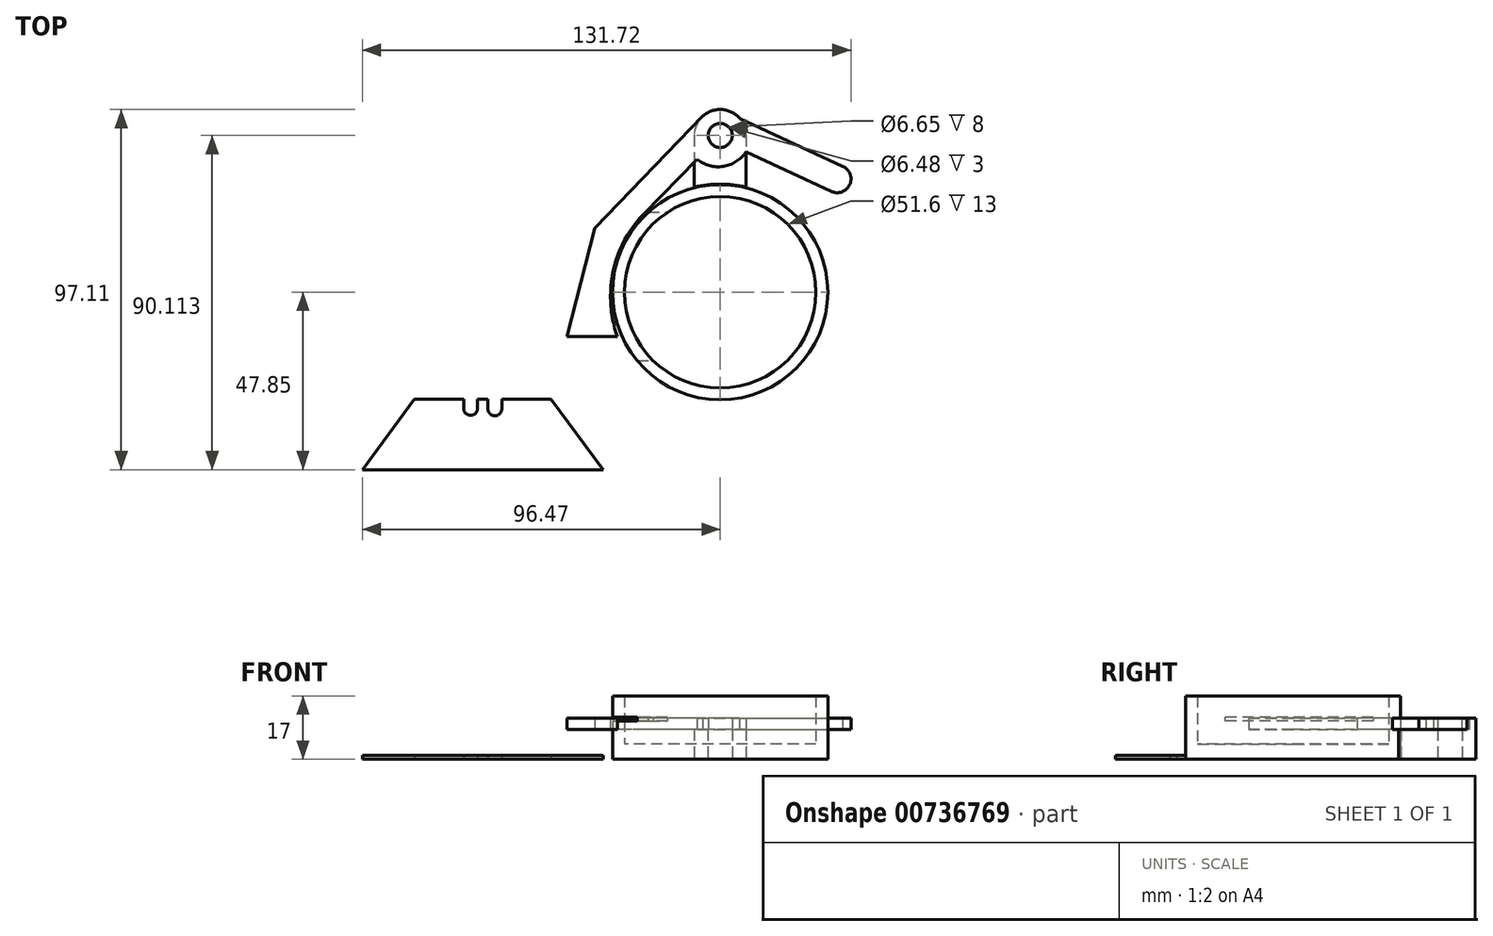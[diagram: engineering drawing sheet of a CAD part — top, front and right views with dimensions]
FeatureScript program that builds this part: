
annotation { "Feature Type Name" : "Feature", "Feature Type Description" : "" }
export const myFeature = defineFeature(function(context is Context, id is Id, definition is map)
    precondition{}
    {
        {
            var Q0;
            Q0=qCreatedBy(makeId("Top.planeOp"),FACE);
            var sketch = newSketch(context, id + "F0", { "sketchPlane" : qUnion([Q0])});
            skCircle(sketch, "E0", {"center": v(0, 0) * mm, "radius": 25.8 * mm});
            skCircle(sketch, "E1", {"center": v(0, 0) * mm, "radius": 29 * mm});
            skSolve(sketch);
        }
        {
            var Q0;
            Q0=makeQuery(id+"F0.imprint","IMPRINT",FACE,{"disambiguationData":[TD([[makeQuery(id+"F0.imprint","IMPRINT",EDGE,{"derivedFrom":sQuery(id+"F0.wireOp",EDGE,"E0")}),1.0]])]});
            extrude(context, id + "F1", {"entities" : qUnion([Q0]), "depth" : 4 * mm, "offsetDistance" : 25 * mm});
        }
        {
            var Q0;
            Q0 = qSketchRegion(id + "F0", true);
            extrude(context, id + "F2", {"entities" : qUnion([Q0]), "operationType" : NewBodyOperationType.ADD, "depth" : 17 * mm, "offsetDistance" : 25 * mm});
        }
        {
            var Q0;
            Q0=qCreatedBy(makeId("Right.planeOp"),FACE);
            var sketch = newSketch(context, id + "F3", { "sketchPlane" : qUnion([Q0])});
            skLineSegment(sketch, "E2.bottom", {"start": v(21.55, 11.3) * mm, "end": v(-18.45, 11.3) * mm});
            skLineSegment(sketch, "E2.top", {"start": v(21.55, 10.3) * mm, "end": v(-18.45, 10.3) * mm});
            skLineSegment(sketch, "E2.left", {"start": v(21.55, 11.3) * mm, "end": v(21.55, 10.3) * mm});
            skLineSegment(sketch, "E2.right", {"start": v(-18.45, 11.3) * mm, "end": v(-18.45, 10.3) * mm});
            skSolve(sketch);
        }
        {
            var Q0;
            Q0 = qSketchRegion(id + "F3", true);
            extrude(context, id + "F4", {"entities" : qUnion([Q0]), "operationType" : NewBodyOperationType.REMOVE, "oppositeDirection" : true, "depth" : 50 * mm, "offsetDistance" : 25 * mm});
        }
        {
            var Q0;
            Q0=qCreatedBy(makeId("Top.planeOp"),FACE);
            var sketch = newSketch(context, id + "F5", { "sketchPlane" : qUnion([Q0])});
            skLineSegment(sketch, "E3", {"start": v(0, 29.34) * mm, "end": v(0, 55.19) * mm, "construction": true});
            skLineSegment(sketch, "E4", {"start": v(0, 42.26) * mm, "end": v(-57.48, 42.26) * mm, "construction": true});
            skLineSegment(sketch, "E5", {"start": v(0, 42.26) * mm, "end": v(55.1, 42.26) * mm, "construction": true});
            skCircle(sketch, "E6", {"center": v(0, 42.26) * mm, "radius": 7 * mm, "construction": true});
            skLineSegment(sketch, "E7", {"start": v(0, 42.26) * mm, "end": v(-16.78, -23.1) * mm, "construction": true});
            skLineSegment(sketch, "E8", {"start": v(-7, 42.26) * mm, "end": v(-7, 28.42) * mm});
            skLineSegment(sketch, "E9", {"start": v(7, 42.26) * mm, "end": v(7, 28.42) * mm});
            skArc(sketch, "E10", {"start": v(7, 42.26) * mm, "mid": v(0, 49.26) * mm, "end": v(-7, 42.26) * mm});
            skCircle(sketch, "E11", {"center": v(0, 42.26) * mm, "radius": 3.32 * mm});
            skArc(sketch, "E12", {"start": v(7, 28.42) * mm, "mid": v(0, 29.14) * mm, "end": v(-7, 28.42) * mm});
            skSolve(sketch);
        }
        {
            var Q0;
            Q0 = qSketchRegion(id + "F5", true);
            extrude(context, id + "F6", {"entities" : qUnion([Q0]), "operationType" : NewBodyOperationType.ADD, "depth" : 8 * mm, "offsetDistance" : 25 * mm});
        }
        {
            var Q0;
            Q0=makeQuery(id+"F6.opExtrude","CAP_FACE",FACE,{"disambiguationData":[OSD([sQuery(id+"F5.wireOp",EDGE,"E8"),sQuery(id+"F5.wireOp",EDGE,"E9"),sQuery(id+"F5.wireOp",EDGE,"E10"),sQuery(id+"F5.wireOp",EDGE,"E11"),sQuery(id+"F5.wireOp",EDGE,"E12")])],"isStart":false});
            var sketch = newSketch(context, id + "F7", { "sketchPlane" : qUnion([Q0])});
            skCircle(sketch, "E13", {"center": v(0, 42.26) * mm, "radius": 3.24 * mm});
            skLineSegment(sketch, "E14", {"start": v(-46.76, 42.26) * mm, "end": v(42.2, 42.26) * mm, "construction": true});
            skLineSegment(sketch, "E15", {"start": v(-4.7, 47.44) * mm, "end": v(-33.77, 17.23) * mm});
            skLineSegment(sketch, "E16", {"start": v(5.25, 46.88) * mm, "end": v(33.24, 33.83) * mm});
            skArc(sketch, "E17", {"start": v(5.25, 46.88) * mm, "mid": v(0.39, 49.24) * mm, "end": v(-4.7, 47.44) * mm});
            skArc(sketch, "E18", {"start": v(-6.23, 35.86) * mm, "mid": v(0.83, 33.93) * mm, "end": v(7, 37.89) * mm});
            skLineSegment(sketch, "E19", {"start": v(-6.23, 35.86) * mm, "end": v(-20.57, 21.13) * mm});
            skLineSegment(sketch, "E20", {"start": v(7, 37.89) * mm, "end": v(29.98, 27.17) * mm});
            skArc(sketch, "E21", {"start": v(29.98, 27.17) * mm, "mid": v(34.94, 29.03) * mm, "end": v(32.98, 33.95) * mm});
            skArc(sketch, "E22", {"start": v(-20.57, 21.13) * mm, "mid": v(-27.04, 11.4) * mm, "end": v(-29.55, 0) * mm});
            skPoint(sketch, "E23.orphan", {"position": v(-50.35, 0) * mm});
            skLineSegment(sketch, "E24", {"start": v(-27.73, -11.98) * mm, "end": v(-41.46, -11.98) * mm});
            skLineSegment(sketch, "E25", {"start": v(-41.34, -11.98) * mm, "end": v(-41.46, -11.98) * mm});
            skArc(sketch, "E26", {"start": v(-29.55, 0) * mm, "mid": v(-29.2, -6.08) * mm, "end": v(-27.73, -11.98) * mm});
            skLineSegment(sketch, "E27", {"start": v(-41.34, -11.98) * mm, "end": v(-33.77, 17.23) * mm});
            skSolve(sketch);
        }
        {
            var Q0;
            Q0 = qSketchRegion(id + "F7", true);
            extrude(context, id + "F8", {"entities" : qUnion([Q0]), "operationType" : NewBodyOperationType.ADD, "depth" : 3 * mm, "offsetDistance" : 25 * mm});
        }
        {
            var Q0;
            Q0=qCreatedBy(makeId("Top.planeOp"),FACE);
            var sketch = newSketch(context, id + "F9", { "sketchPlane" : qUnion([Q0])});
            skLineSegment(sketch, "E28.bottom", {"start": v(-82.47, -28.85) * mm, "end": v(-69.16, -28.85) * mm});
            skLineSegment(sketch, "E28.top", {"start": v(-96.47, -47.85) * mm, "end": v(-31.55, -47.85) * mm});
            skLineSegment(sketch, "E29", {"start": v(-96.47, -47.85) * mm, "end": v(-82.47, -28.85) * mm});
            skLineSegment(sketch, "E30", {"start": v(-45.55, -28.85) * mm, "end": v(-31.55, -47.85) * mm});
            skArc(sketch, "E31", {"start": v(-69.16, -31.35) * mm, "mid": v(-67.29, -33.18) * mm, "end": v(-65.41, -31.35) * mm});
            skArc(sketch, "E32", {"start": v(-62.61, -31.35) * mm, "mid": v(-60.74, -33.3) * mm, "end": v(-58.86, -31.35) * mm});
            skLineSegment(sketch, "E33", {"start": v(-69.16, -28.85) * mm, "end": v(-69.16, -31.35) * mm});
            skLineSegment(sketch, "E34", {"start": v(-65.41, -28.85) * mm, "end": v(-65.41, -31.35) * mm});
            skLineSegment(sketch, "E35", {"start": v(-62.61, -28.85) * mm, "end": v(-62.61, -31.35) * mm});
            skLineSegment(sketch, "E36", {"start": v(-58.86, -28.85) * mm, "end": v(-58.86, -31.35) * mm});
            skLineSegment(sketch, "E37.trimOffspring", {"start": v(-65.41, -28.85) * mm, "end": v(-62.61, -28.85) * mm});
            skLineSegment(sketch, "E38.trimOffspring", {"start": v(-58.86, -28.85) * mm, "end": v(-45.55, -28.85) * mm});
            skSolve(sketch);
        }
        {
            var Q0;
            Q0 = qSketchRegion(id + "F9", true);
            extrude(context, id + "F10", {"entities" : qUnion([Q0]), "depth" : 1 * mm, "offsetDistance" : 25 * mm});
        }
    });
